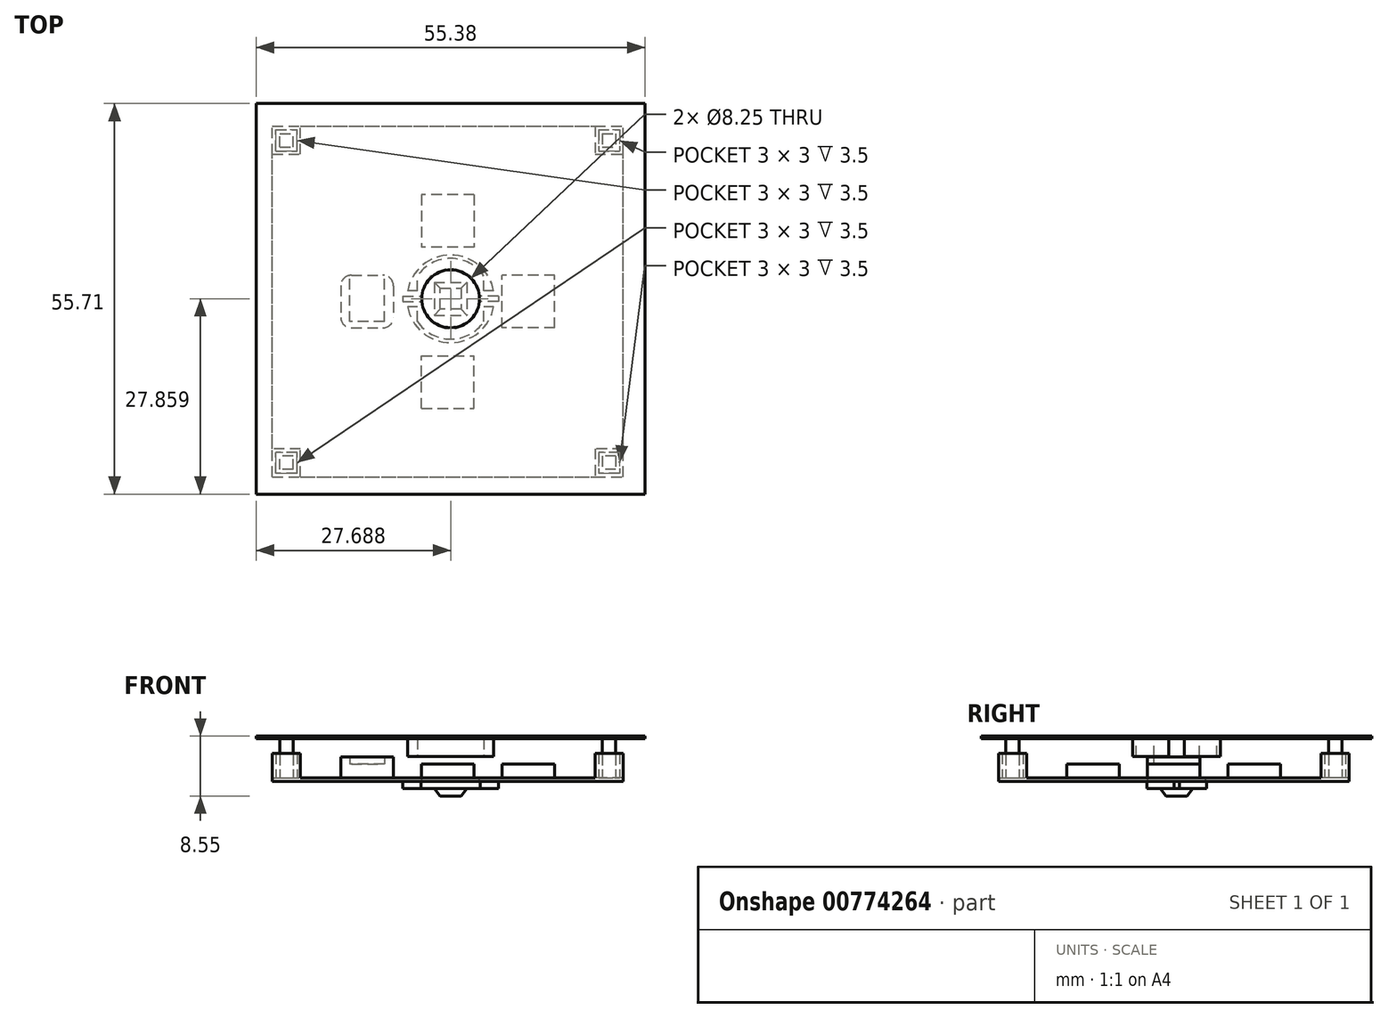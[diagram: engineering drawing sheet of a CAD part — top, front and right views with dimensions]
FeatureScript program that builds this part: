
annotation { "Feature Type Name" : "Feature", "Feature Type Description" : "" }
export const myFeature = defineFeature(function(context is Context, id is Id, definition is map)
    precondition{}
    {
        {
            var Q0;
            Q0=qCreatedBy(makeId("Top.planeOp"),FACE);
            var sketch = newSketch(context, id + "F0", { "sketchPlane" : qUnion([Q0])});
            skLineSegment(sketch, "E0.bottom", {"start": v(0, 0) * mm, "end": v(50, 0) * mm});
            skLineSegment(sketch, "E0.top", {"start": v(0, 50) * mm, "end": v(50, 50) * mm});
            skLineSegment(sketch, "E0.left", {"start": v(0, 0) * mm, "end": v(0, 50) * mm});
            skLineSegment(sketch, "E0.right", {"start": v(50, 0) * mm, "end": v(50, 50) * mm});
            skSolve(sketch);
        }
        {
            var Q0;
            Q0=makeQuery(id+"F0.imprint","IMPRINT",FACE,{"disambiguationData":[TD([[makeQuery(id+"F0.imprint","IMPRINT",EDGE,{"derivedFrom":sQuery(id+"F0.wireOp",EDGE,"E0.bottom")}),1.0]])]});
            extrude(context, id + "F1", {"entities" : qUnion([Q0]), "depth" : 0.5 * mm, "offsetDistance" : 25 * mm});
        }
        {
            var Q0;
            Q0=makeQuery(id+"F1.opExtrude","CAP_FACE",FACE,{"disambiguationData":[OSD([sQuery(id+"F0.wireOp",EDGE,"E0.bottom"),sQuery(id+"F0.wireOp",EDGE,"E0.top"),sQuery(id+"F0.wireOp",EDGE,"E0.left"),sQuery(id+"F0.wireOp",EDGE,"E0.right")])],"isStart":false});
            var sketch = newSketch(context, id + "F2", { "sketchPlane" : qUnion([Q0])});
            skLineSegment(sketch, "E1.bottom", {"start": v(46.5, 49.5) * mm, "end": v(49.5, 49.5) * mm});
            skLineSegment(sketch, "E1.top", {"start": v(46.5, 46.5) * mm, "end": v(49.5, 46.5) * mm});
            skLineSegment(sketch, "E1.left", {"start": v(46.5, 49.5) * mm, "end": v(46.5, 46.5) * mm});
            skLineSegment(sketch, "E1.right", {"start": v(49.5, 49.5) * mm, "end": v(49.5, 46.5) * mm});
            skPoint(sketch, "E2.middle.positionSnap0", {"position": v(49.5, 48) * mm});
            skPoint(sketch, "E2.middle.positionSnap1", {"position": v(48, 49.5) * mm});
            skPoint(sketch, "E2.centerSnap0", {"position": v(49.5, 48) * mm});
            skPoint(sketch, "E2.centerSnap1", {"position": v(48, 49.5) * mm});
            skLineSegment(sketch, "E3.0", {"start": v(46, 50) * mm, "end": v(50, 50) * mm});
            skLineSegment(sketch, "E3.1", {"start": v(46, 50) * mm, "end": v(46, 46) * mm});
            skLineSegment(sketch, "E3.2", {"start": v(46, 46) * mm, "end": v(50, 46) * mm});
            skLineSegment(sketch, "E3.3", {"start": v(50, 50) * mm, "end": v(50, 46) * mm});
            skLineSegment(sketch, "E4.0", {"start": v(47.05, 48.95) * mm, "end": v(48.95, 48.95) * mm});
            skLineSegment(sketch, "E4.1", {"start": v(47.05, 48.95) * mm, "end": v(47.05, 47.05) * mm});
            skLineSegment(sketch, "E4.2", {"start": v(47.05, 47.05) * mm, "end": v(48.95, 47.05) * mm});
            skLineSegment(sketch, "E4.3", {"start": v(48.95, 48.95) * mm, "end": v(48.95, 47.05) * mm});
            skLineSegment(sketch, "E5.1.0", {"start": v(0, 50) * mm, "end": v(4, 50) * mm});
            skLineSegment(sketch, "E5.1.1", {"start": v(4, 46) * mm, "end": v(4, 50) * mm});
            skLineSegment(sketch, "E5.1.2", {"start": v(0, 46) * mm, "end": v(4, 46) * mm});
            skLineSegment(sketch, "E5.1.3", {"start": v(1.05, 47.05) * mm, "end": v(2.95, 47.05) * mm});
            skLineSegment(sketch, "E5.1.4", {"start": v(3.5, 46.5) * mm, "end": v(3.5, 49.5) * mm});
            skLineSegment(sketch, "E5.1.5", {"start": v(0, 46) * mm, "end": v(0, 50) * mm});
            skLineSegment(sketch, "E5.1.6", {"start": v(2.95, 47.05) * mm, "end": v(2.95, 48.95) * mm});
            skLineSegment(sketch, "E5.1.7", {"start": v(0.5, 46.5) * mm, "end": v(3.5, 46.5) * mm});
            skPoint(sketch, "E5.1.8", {"position": v(2, 49.5) * mm});
            skLineSegment(sketch, "E5.1.9", {"start": v(1.05, 47.05) * mm, "end": v(1.05, 48.95) * mm});
            skPoint(sketch, "E5.1.10", {"position": v(0.5, 48) * mm});
            skPoint(sketch, "E5.1.11", {"position": v(2, 49.5) * mm});
            skLineSegment(sketch, "E5.1.12", {"start": v(0.5, 46.5) * mm, "end": v(0.5, 49.5) * mm});
            skPoint(sketch, "E5.1.13", {"position": v(0.5, 48) * mm});
            skLineSegment(sketch, "E5.1.14", {"start": v(1.05, 48.95) * mm, "end": v(2.95, 48.95) * mm});
            skLineSegment(sketch, "E5.1.15", {"start": v(0.5, 49.5) * mm, "end": v(3.5, 49.5) * mm});
            skLineSegment(sketch, "E5.2.0", {"start": v(0, 0) * mm, "end": v(0, 4) * mm});
            skLineSegment(sketch, "E5.2.1", {"start": v(4, 4) * mm, "end": v(0, 4) * mm});
            skLineSegment(sketch, "E5.2.2", {"start": v(4, 0) * mm, "end": v(4, 4) * mm});
            skLineSegment(sketch, "E5.2.3", {"start": v(2.95, 1.05) * mm, "end": v(2.95, 2.95) * mm});
            skLineSegment(sketch, "E5.2.4", {"start": v(3.5, 3.5) * mm, "end": v(0.5, 3.5) * mm});
            skLineSegment(sketch, "E5.2.5", {"start": v(4, 0) * mm, "end": v(0, 0) * mm});
            skLineSegment(sketch, "E5.2.6", {"start": v(2.95, 2.95) * mm, "end": v(1.05, 2.95) * mm});
            skLineSegment(sketch, "E5.2.7", {"start": v(3.5, 0.5) * mm, "end": v(3.5, 3.5) * mm});
            skPoint(sketch, "E5.2.8", {"position": v(0.5, 2) * mm});
            skLineSegment(sketch, "E5.2.9", {"start": v(2.95, 1.05) * mm, "end": v(1.05, 1.05) * mm});
            skPoint(sketch, "E5.2.10", {"position": v(2, 0.5) * mm});
            skPoint(sketch, "E5.2.11", {"position": v(0.5, 2) * mm});
            skLineSegment(sketch, "E5.2.12", {"start": v(3.5, 0.5) * mm, "end": v(0.5, 0.5) * mm});
            skPoint(sketch, "E5.2.13", {"position": v(2, 0.5) * mm});
            skLineSegment(sketch, "E5.2.14", {"start": v(1.05, 1.05) * mm, "end": v(1.05, 2.95) * mm});
            skLineSegment(sketch, "E5.2.15", {"start": v(0.5, 0.5) * mm, "end": v(0.5, 3.5) * mm});
            skLineSegment(sketch, "E5.3.0", {"start": v(50, 0) * mm, "end": v(46, 0) * mm});
            skLineSegment(sketch, "E5.3.1", {"start": v(46, 4) * mm, "end": v(46, 0) * mm});
            skLineSegment(sketch, "E5.3.2", {"start": v(50, 4) * mm, "end": v(46, 4) * mm});
            skLineSegment(sketch, "E5.3.3", {"start": v(48.95, 2.95) * mm, "end": v(47.05, 2.95) * mm});
            skLineSegment(sketch, "E5.3.4", {"start": v(46.5, 3.5) * mm, "end": v(46.5, 0.5) * mm});
            skLineSegment(sketch, "E5.3.5", {"start": v(50, 4) * mm, "end": v(50, 0) * mm});
            skLineSegment(sketch, "E5.3.6", {"start": v(47.05, 2.95) * mm, "end": v(47.05, 1.05) * mm});
            skLineSegment(sketch, "E5.3.7", {"start": v(49.5, 3.5) * mm, "end": v(46.5, 3.5) * mm});
            skPoint(sketch, "E5.3.8", {"position": v(48, 0.5) * mm});
            skLineSegment(sketch, "E5.3.9", {"start": v(48.95, 2.95) * mm, "end": v(48.95, 1.05) * mm});
            skPoint(sketch, "E5.3.10", {"position": v(49.5, 2) * mm});
            skPoint(sketch, "E5.3.11", {"position": v(48, 0.5) * mm});
            skLineSegment(sketch, "E5.3.12", {"start": v(49.5, 3.5) * mm, "end": v(49.5, 0.5) * mm});
            skPoint(sketch, "E5.3.13", {"position": v(49.5, 2) * mm});
            skLineSegment(sketch, "E5.3.14", {"start": v(48.95, 1.05) * mm, "end": v(47.05, 1.05) * mm});
            skLineSegment(sketch, "E5.3.15", {"start": v(49.5, 0.5) * mm, "end": v(46.5, 0.5) * mm});
            skPoint(sketch, "E5.center", {"position": v(25, 25) * mm});
            skSolve(sketch);
        }
        {
            var Q0;
            Q0=makeQuery(id+"F2.imprint","IMPRINT",FACE,{"disambiguationData":[TD([[makeQuery(id+"F2.imprint","IMPRINT",EDGE,{"derivedFrom":sQuery(id+"F2.wireOp",EDGE,"E1.bottom")}),1.0]])]});
            var Q1;
            Q1=makeQuery(id+"F2.imprint","IMPRINT",FACE,{"disambiguationData":[TD([[makeQuery(id+"F2.imprint","IMPRINT",EDGE,{"derivedFrom":sQuery(id+"F2.wireOp",EDGE,"E5.1.0")}),-1.0]])]});
            var Q2;
            Q2=makeQuery(id+"F2.imprint","IMPRINT",FACE,{"disambiguationData":[TD([[makeQuery(id+"F2.imprint","IMPRINT",EDGE,{"derivedFrom":sQuery(id+"F2.wireOp",EDGE,"E5.2.0")}),-1.0]])]});
            var Q3;
            Q3=makeQuery(id+"F2.imprint","IMPRINT",FACE,{"disambiguationData":[TD([[makeQuery(id+"F2.imprint","IMPRINT",EDGE,{"derivedFrom":sQuery(id+"F2.wireOp",EDGE,"E5.3.0")}),-1.0]])]});
            var Q4;
            Q4=makeQuery(id+"F2.imprint","IMPRINT",FACE,{"disambiguationData":[TD([[makeQuery(id+"F2.imprint","IMPRINT",EDGE,{"derivedFrom":sQuery(id+"F2.wireOp",EDGE,"E5.3.0")}),1.0]])]});
            extrude(context, id + "F3", {"entities" : qUnion([Q0, Q1, Q2, Q3, Q4]), "operationType" : NewBodyOperationType.ADD, "depth" : 3.5 * mm, "offsetDistance" : 25 * mm});
        }
        {
            var Q0;
            Q0=makeQuery(id+"F2.imprint","IMPRINT",FACE,{"disambiguationData":[TD([[makeQuery(id+"F2.imprint","IMPRINT",EDGE,{"derivedFrom":sQuery(id+"F2.wireOp",EDGE,"E5.1.3")}),1.0]])]});
            var Q1;
            Q1=makeQuery(id+"F2.imprint","IMPRINT",FACE,{"disambiguationData":[TD([[makeQuery(id+"F2.imprint","IMPRINT",EDGE,{"derivedFrom":sQuery(id+"F2.wireOp",EDGE,"E4.0")}),-1.0]])]});
            var Q2;
            Q2=makeQuery(id+"F2.imprint","IMPRINT",FACE,{"disambiguationData":[TD([[makeQuery(id+"F2.imprint","IMPRINT",EDGE,{"derivedFrom":sQuery(id+"F2.wireOp",EDGE,"E5.3.3")}),1.0]])]});
            var Q3;
            Q3=makeQuery(id+"F2.imprint","IMPRINT",FACE,{"disambiguationData":[TD([[makeQuery(id+"F2.imprint","IMPRINT",EDGE,{"derivedFrom":sQuery(id+"F2.wireOp",EDGE,"E5.2.3")}),1.0]])]});
            extrude(context, id + "F4", {"entities" : qUnion([Q0, Q1, Q2, Q3]), "depth" : 6 * mm, "offsetDistance" : 25 * mm});
        }
        {
            var Q0;
            Q0=makeQuery(id+"F4.opExtrude","CAP_FACE",FACE,{"disambiguationData":[OSD([sQuery(id+"F2.wireOp",EDGE,"E4.0"),sQuery(id+"F2.wireOp",EDGE,"E4.1"),sQuery(id+"F2.wireOp",EDGE,"E4.2"),sQuery(id+"F2.wireOp",EDGE,"E4.3")])],"isStart":false});
            var sketch = newSketch(context, id + "F5", { "sketchPlane" : qUnion([Q0])});
            skLineSegment(sketch, "E6.bottom", {"start": v(53.1, 53.25) * mm, "end": v(-2.28, 53.25) * mm});
            skLineSegment(sketch, "E6.top", {"start": v(53.1, -2.46) * mm, "end": v(-2.28, -2.46) * mm});
            skLineSegment(sketch, "E6.left", {"start": v(53.1, 53.25) * mm, "end": v(53.1, -2.46) * mm});
            skLineSegment(sketch, "E6.right", {"start": v(-2.28, 53.25) * mm, "end": v(-2.28, -2.46) * mm});
            skSolve(sketch);
        }
        {
            var Q0;
            Q0=makeQuery(id+"F5.imprint","IMPRINT",FACE,{"disambiguationData":[TD([[makeQuery(id+"F5.imprint","IMPRINT",EDGE,{"derivedFrom":sQuery(id+"F5.wireOp",EDGE,"E6.bottom")}),1.0]])]});
            extrude(context, id + "F6", {"entities" : qUnion([Q0]), "operationType" : NewBodyOperationType.ADD, "oppositeDirection" : true, "depth" : 0.4 * mm, "offsetDistance" : 25 * mm});
        }
        {
            var Q0;
            {var subQ0=sQuery(id+"F2.wireOp",EDGE,"E4.3");var subQ1=sQuery(id+"F2.wireOp",EDGE,"E4.2");var subQ2=sQuery(id+"F2.wireOp",EDGE,"E4.1");var subQ3=sQuery(id+"F2.wireOp",EDGE,"E4.0");Q0=makeQuery(id+"F6.boolean.opBoolean","MERGE",FACE,{"derivedFrom":[makeQuery(id+"F4.opExtrude","CAP_FACE",FACE,{"disambiguationData":[OSD([subQ3,subQ2,subQ1,subQ0])],"isStart":false}),makeQuery(id+"F4.opExtrude","CAP_FACE",FACE,{"disambiguationData":[OSD([sQuery(id+"F2.wireOp",EDGE,"E5.1.3"),sQuery(id+"F2.wireOp",EDGE,"E5.1.6"),sQuery(id+"F2.wireOp",EDGE,"E5.1.9"),sQuery(id+"F2.wireOp",EDGE,"E5.1.14")])],"isStart":false}),makeQuery(id+"F4.opExtrude","CAP_FACE",FACE,{"disambiguationData":[OSD([sQuery(id+"F2.wireOp",EDGE,"E5.2.3"),sQuery(id+"F2.wireOp",EDGE,"E5.2.6"),sQuery(id+"F2.wireOp",EDGE,"E5.2.9"),sQuery(id+"F2.wireOp",EDGE,"E5.2.14")])],"isStart":false}),makeQuery(id+"F4.opExtrude","CAP_FACE",FACE,{"disambiguationData":[OSD([sQuery(id+"F2.wireOp",EDGE,"E5.3.3"),sQuery(id+"F2.wireOp",EDGE,"E5.3.6"),sQuery(id+"F2.wireOp",EDGE,"E5.3.9"),sQuery(id+"F2.wireOp",EDGE,"E5.3.14")])],"isStart":false}),makeQuery(id+"F6.opExtrude","CAP_FACE",FACE,{"disambiguationData":[OSD([subQ3,subQ2,subQ1,subQ0,sQuery(id+"F5.wireOp",EDGE,"E6.bottom"),sQuery(id+"F5.wireOp",EDGE,"E6.top"),sQuery(id+"F5.wireOp",EDGE,"E6.left"),sQuery(id+"F5.wireOp",EDGE,"E6.right")])],"isStart":true})]});}
            var sketch = newSketch(context, id + "F7", { "sketchPlane" : qUnion([Q0])});
            skCircle(sketch, "E7", {"center": v(25.4, 25.4) * mm, "radius": 4.12 * mm});
            skPoint(sketch, "E7.centerSnap0", {"position": v(25.4, 53.25) * mm});
            skPoint(sketch, "E7.centerSnap1", {"position": v(53.1, 25.4) * mm});
            skSolve(sketch);
        }
        {
            var Q0;
            Q0=makeQuery(id+"F7.imprint","IMPRINT",FACE,{"disambiguationData":[TD([[makeQuery(id+"F7.imprint","IMPRINT",EDGE,{"derivedFrom":sQuery(id+"F7.wireOp",EDGE,"E7")}),1.0]])]});
            extrude(context, id + "F8", {"entities" : qUnion([Q0]), "operationType" : NewBodyOperationType.REMOVE, "oppositeDirection" : true, "depth" : 25 * mm, "offsetDistance" : 25 * mm});
        }
        {
            var Q0;
            Q0=makeQuery(id+"FnoxdWEcKo2KXdU_3.boolean.opBoolean","MERGE",FACE,{"derivedFrom":[makeQuery(id+"F6.opExtrude","CAP_FACE",FACE,{"disambiguationData":[OSD([sQuery(id+"F2.wireOp",EDGE,"E4.0"),sQuery(id+"F2.wireOp",EDGE,"E4.1"),sQuery(id+"F2.wireOp",EDGE,"E4.2"),sQuery(id+"F2.wireOp",EDGE,"E4.3"),sQuery(id+"F5.wireOp",EDGE,"E6.bottom"),sQuery(id+"F5.wireOp",EDGE,"E6.top"),sQuery(id+"F5.wireOp",EDGE,"E6.left"),sQuery(id+"F5.wireOp",EDGE,"E6.right")])],"isStart":false}),makeQuery(id+"FnoxdWEcKo2KXdU_3.opExtrude","SWEPT_FACE",FACE,{"disambiguationData":[OSD([sQuery(id+"F0zA4uYZW5pRUPb_3.wireOp",EDGE,"ZhX8Fjgi-kqvp-VlpE-l4Rn-IeRyZbtZChRy.bottom")])]})]});
            var sketch = newSketch(context, id + "F9", { "sketchPlane" : qUnion([Q0])});
            skLineSegment(sketch, "E8", {"start": v(25.4, -25.4) * mm, "end": v(29.53, -25.4) * mm});
            skCircle(sketch, "E9", {"center": v(25.4, -25.4) * mm, "radius": 5.75 * mm});
            skCircle(sketch, "E10", {"center": v(25.4, -25.4) * mm, "radius": 6.25 * mm});
            skLineSegment(sketch, "E11", {"start": v(30.16, -22.16) * mm, "end": v(30.16, -28.64) * mm});
            skLineSegment(sketch, "E12", {"start": v(20.66, -22.16) * mm, "end": v(20.66, -28.64) * mm});
            skSolve(sketch);
        }
        {
            var Q0;
            {var subQ0=sQuery(id+"F9.wireOp",EDGE,"scZHxu3C-Op0m-khkx-aFYf-Y6gfYPpbK4Jl");Q0=makeQuery(id+"F9.imprint","IMPRINT",FACE,{"disambiguationData":[TD([[makeQuery(id+"F9.imprint","IMPRINT",EDGE,{"derivedFrom":subQ0}),-1.0]])]});}
            var Q1;
            Q1=makeQuery(id+"F9.imprint","IMPRINT",FACE,{"disambiguationData":[TD([[makeQuery(id+"F9.imprint","IMPRINT",EDGE,{"derivedFrom":sQuery(id+"F9.wireOp",EDGE,"TZnjQXDI-6Li4-iHBg-k0Ms-UXLXTafPAAUR")}),-1.0]])]});
            var Q2;
            {var subQ5=sQuery(id+"F9.wireOp",EDGE,"F097BGmS-OGrE-Bj6g-8D74-8TD7AIuaI6WG");Q2=makeQuery(id+"F9.imprint","IMPRINT",FACE,{"disambiguationData":[TD([[makeQuery(id+"F9.imprint","IMPRINT",EDGE,{"derivedFrom":subQ5}),1.0]])]});}
            var Q3;
            {var subQ0=sQuery(id+"F9.wireOp",EDGE,"7kH5QydC-Tvzd-wKTz-Q8G2-IkZKPWhglS4Q");Q3=makeQuery(id+"F9.imprint","IMPRINT",FACE,{"disambiguationData":[TD([[makeQuery(id+"F9.imprint","IMPRINT",EDGE,{"derivedFrom":subQ0}),-1.0]])]});}
            var Q4;
            Q4=makeQuery(id+"F9.imprint","IMPRINT",FACE,{"disambiguationData":[TD([[makeQuery(id+"F9.imprint","IMPRINT",EDGE,{"derivedFrom":sQuery(id+"F9.wireOp",EDGE,"E10")}),1.0]])]});
            var Q5;
            {var subQ0=sQuery(id+"F9.wireOp",EDGE,"E11");Q5=makeQuery(id+"F9.imprint","IMPRINT",FACE,{"disambiguationData":[TD([[makeQuery(id+"F9.imprint","IMPRINT",EDGE,{"derivedFrom":subQ0}),1.0]])]});}
            var Q6;
            {var subQ0=sQuery(id+"F9.wireOp",EDGE,"XEGzPRrg-yoOm-QcLb-v5r6-et9ivG9pCGP1");Q6=makeQuery(id+"F9.imprint","IMPRINT",FACE,{"disambiguationData":[TD([[makeQuery(id+"F9.imprint","IMPRINT",EDGE,{"derivedFrom":subQ0}),1.0]])]});}
            var Q7;
            {var subQ0=sQuery(id+"F9.wireOp",EDGE,"23869d93-fd9b-4a96-a758-ed1db567c41d");Q7=makeQuery(id+"F9.imprint","IMPRINT",FACE,{"disambiguationData":[TD([[makeQuery(id+"F9.imprint","IMPRINT",EDGE,{"derivedFrom":subQ0}),-1.0]])]});}
            var Q8;
            {var subQ0=sQuery(id+"F9.wireOp",EDGE,"E12");Q8=makeQuery(id+"F9.imprint","IMPRINT",FACE,{"disambiguationData":[TD([[makeQuery(id+"F9.imprint","IMPRINT",EDGE,{"derivedFrom":subQ0}),-1.0]])]});}
            extrude(context, id + "F10", {"entities" : qUnion([Q0, Q1, Q2, Q3, Q4, Q5, Q6, Q7, Q8]), "operationType" : NewBodyOperationType.ADD, "depth" : 2.5 * mm, "offsetDistance" : 25 * mm});
        }
        {
            var Q0;
            {var subQ0=sQuery(id+"F0.wireOp",EDGE,"E0.bottom");var subQ1=sQuery(id+"F0.wireOp",EDGE,"E0.right");var subQ2=sQuery(id+"F0.wireOp",EDGE,"E0.top");var subQ3=sQuery(id+"F0.wireOp",EDGE,"E0.left");Q0=makeQuery(id+"F3.boolean.opBoolean","SPLIT",FACE,{"disambiguationData":[TD([makeQuery(id+"F1.opExtrude","SWEPT_FACE",FACE,{"disambiguationData":[OSD([subQ0])]})])],"derivedFrom":makeQuery(id+"F1.opExtrude","CAP_FACE",FACE,{"disambiguationData":[OSD([subQ0,subQ2,subQ3,subQ1])],"isStart":false})});}
            var sketch = newSketch(context, id + "F11", { "sketchPlane" : qUnion([Q0])});
            skLineSegment(sketch, "E13.bottom", {"start": v(9.75, 28.75) * mm, "end": v(17.25, 28.75) * mm});
            skLineSegment(sketch, "E13.top", {"start": v(9.75, 21.25) * mm, "end": v(17.25, 21.25) * mm});
            skLineSegment(sketch, "E13.left", {"start": v(9.75, 28.75) * mm, "end": v(9.75, 21.25) * mm});
            skLineSegment(sketch, "E13.right", {"start": v(17.25, 28.75) * mm, "end": v(17.25, 21.25) * mm});
            skPoint(sketch, "E13.middle.positionSnap0", {"position": v(0, 25) * mm});
            skPoint(sketch, "E13.middle.positionSnap1", {"position": v(25, 0) * mm});
            skPoint(sketch, "E13.centerSnap0", {"position": v(0, 25) * mm});
            skPoint(sketch, "E13.centerSnap1", {"position": v(25, 0) * mm});
            skPoint(sketch, "E14", {"position": v(13.5, 25) * mm});
            skPoint(sketch, "E15", {"position": v(13.5, 21.25) * mm});
            skPoint(sketch, "E16", {"position": v(17.25, 25) * mm});
            skLineSegment(sketch, "E17", {"start": v(0, 25) * mm, "end": v(25, 25) * mm});
            skPoint(sketch, "E17.endSnap0", {"position": v(25, 50) * mm});
            skLineSegment(sketch, "E18.1.0", {"start": v(21.25, 9.75) * mm, "end": v(21.25, 17.25) * mm});
            skLineSegment(sketch, "E18.1.1", {"start": v(21.25, 9.75) * mm, "end": v(28.75, 9.75) * mm});
            skLineSegment(sketch, "E18.1.2", {"start": v(21.25, 17.25) * mm, "end": v(28.75, 17.25) * mm});
            skLineSegment(sketch, "E18.1.3", {"start": v(28.75, 9.75) * mm, "end": v(28.75, 17.25) * mm});
            skLineSegment(sketch, "E18.2.0", {"start": v(40.25, 21.25) * mm, "end": v(32.75, 21.25) * mm});
            skLineSegment(sketch, "E18.2.1", {"start": v(40.25, 21.25) * mm, "end": v(40.25, 28.75) * mm});
            skLineSegment(sketch, "E18.2.2", {"start": v(32.75, 21.25) * mm, "end": v(32.75, 28.75) * mm});
            skLineSegment(sketch, "E18.2.3", {"start": v(40.25, 28.75) * mm, "end": v(32.75, 28.75) * mm});
            skLineSegment(sketch, "E18.3.0", {"start": v(28.75, 40.25) * mm, "end": v(28.75, 32.75) * mm});
            skLineSegment(sketch, "E18.3.1", {"start": v(28.75, 40.25) * mm, "end": v(21.25, 40.25) * mm});
            skLineSegment(sketch, "E18.3.2", {"start": v(28.75, 32.75) * mm, "end": v(21.25, 32.75) * mm});
            skLineSegment(sketch, "E18.3.3", {"start": v(21.25, 40.25) * mm, "end": v(21.25, 32.75) * mm});
            skPoint(sketch, "E18.center", {"position": v(25, 25) * mm});
            skSolve(sketch);
        }
        {
            var Q0;
            Q0=makeQuery(id+"F11.imprint","IMPRINT",FACE,{"disambiguationData":[TD([[makeQuery(id+"F11.imprint","IMPRINT",EDGE,{"derivedFrom":sQuery(id+"F11.wireOp",EDGE,"E13.bottom")}),-1.0]])]});
            var Q1;
            {var subQ0=sQuery(id+"F11.wireOp",EDGE,"E13.top");Q1=makeQuery(id+"F11.imprint","IMPRINT",FACE,{"disambiguationData":[TD([[makeQuery(id+"F11.imprint","IMPRINT",EDGE,{"derivedFrom":subQ0}),1.0]])]});}
            var Q2;
            Q2=makeQuery(id+"F11.imprint","IMPRINT",FACE,{"disambiguationData":[TD([[makeQuery(id+"F11.imprint","IMPRINT",EDGE,{"derivedFrom":sQuery(id+"F11.wireOp",EDGE,"E18.1.0")}),-1.0]])]});
            var Q3;
            Q3=makeQuery(id+"F11.imprint","IMPRINT",FACE,{"disambiguationData":[TD([[makeQuery(id+"F11.imprint","IMPRINT",EDGE,{"derivedFrom":sQuery(id+"F11.wireOp",EDGE,"E18.2.0")}),-1.0]])]});
            var Q4;
            Q4=makeQuery(id+"F11.imprint","IMPRINT",FACE,{"disambiguationData":[TD([[makeQuery(id+"F11.imprint","IMPRINT",EDGE,{"derivedFrom":sQuery(id+"F11.wireOp",EDGE,"E18.3.0")}),-1.0]])]});
            extrude(context, id + "F12", {"entities" : qUnion([Q0, Q1, Q2, Q3, Q4]), "operationType" : NewBodyOperationType.ADD, "depth" : 2 * mm, "offsetDistance" : 25 * mm});
        }
        {
            var Q0;
            Q0=makeQuery(id+"F12.opExtrude","CAP_FACE",FACE,{"disambiguationData":[OSD([sQuery(id+"F11.wireOp",EDGE,"E13.bottom"),sQuery(id+"F11.wireOp",EDGE,"E13.top"),sQuery(id+"F11.wireOp",EDGE,"E13.left"),sQuery(id+"F11.wireOp",EDGE,"E13.right")])],"isStart":false});
            var sketch = newSketch(context, id + "F13", { "sketchPlane" : qUnion([Q0])});
            skLineSegment(sketch, "E19", {"start": v(15.97, 21.25) * mm, "end": v(15.97, 28.75) * mm});
            skLineSegment(sketch, "E20", {"start": v(11.02, 21.25) * mm, "end": v(11.02, 28.75) * mm});
            skLineSegment(sketch, "E21", {"start": v(11.02, 25) * mm, "end": v(9.75, 25) * mm, "construction": true});
            skLineSegment(sketch, "E22", {"start": v(15.97, 25) * mm, "end": v(17.25, 25) * mm, "construction": true});
            skLineSegment(sketch, "E23", {"start": v(15.97, 22.12) * mm, "end": v(11.02, 22.12) * mm});
            skSolve(sketch);
        }
        {
            var Q0;
            {var subQ0=makeQuery(id+"F12.opExtrude","CAP_EDGE",EDGE,{"disambiguationData":[OSD([sQuery(id+"F11.wireOp",EDGE,"E13.right")])],"isStart":false});Q0=makeQuery(id+"F13.imprint","IMPRINT",FACE,{"disambiguationData":[TD([[makeQuery(id+"F13.imprint","IMPRINT",EDGE,{"derivedFrom":subQ0}),-1.0]])]});}
            var Q1;
            {var subQ3=sQuery(id+"F13.wireOp",EDGE,"E23");Q1=makeQuery(id+"F13.imprint","IMPRINT",FACE,{"disambiguationData":[TD([[makeQuery(id+"F13.imprint","IMPRINT",EDGE,{"derivedFrom":subQ3}),1.0]])]});}
            var Q2;
            {var subQ0=makeQuery(id+"F12.opExtrude","CAP_EDGE",EDGE,{"disambiguationData":[OSD([sQuery(id+"F11.wireOp",EDGE,"E13.left")])],"isStart":false});Q2=makeQuery(id+"F13.imprint","IMPRINT",FACE,{"disambiguationData":[TD([[makeQuery(id+"F13.imprint","IMPRINT",EDGE,{"derivedFrom":subQ0}),1.0]])]});}
            extrude(context, id + "F14", {"entities" : qUnion([Q0, Q1, Q2]), "operationType" : NewBodyOperationType.ADD, "depth" : 1 * mm, "offsetDistance" : 25 * mm});
        }
        {
            var Q0;
            {var subQ0=sQuery(id+"F11.wireOp",EDGE,"E13.left");var subQ1=sQuery(id+"F11.wireOp",EDGE,"E13.bottom");Q0=makeQuery(id+"F14.boolean.opBoolean","MERGE",EDGE,{"derivedFrom":[makeQuery(id+"F12.opExtrude","SWEPT_EDGE",EDGE,{"disambiguationData":[OSD([subQ1,subQ0])]}),makeQuery(id+"F14.opExtrude","SWEPT_EDGE",EDGE,{"disambiguationData":[OSD([subQ1,subQ0])]})]});}
            var Q1;
            {var subQ0=sQuery(id+"F11.wireOp",EDGE,"E13.right");var subQ1=sQuery(id+"F11.wireOp",EDGE,"E13.bottom");Q1=makeQuery(id+"F14.boolean.opBoolean","MERGE",EDGE,{"derivedFrom":[makeQuery(id+"F12.opExtrude","SWEPT_EDGE",EDGE,{"disambiguationData":[OSD([subQ1,subQ0])]}),makeQuery(id+"F14.opExtrude","SWEPT_EDGE",EDGE,{"disambiguationData":[OSD([subQ1,subQ0])]})]});}
            var Q2;
            {var subQ0=sQuery(id+"F11.wireOp",EDGE,"E13.right");var subQ1=sQuery(id+"F11.wireOp",EDGE,"E13.top");Q2=makeQuery(id+"F14.boolean.opBoolean","MERGE",EDGE,{"derivedFrom":[makeQuery(id+"F12.opExtrude","SWEPT_EDGE",EDGE,{"disambiguationData":[OSD([subQ1,subQ0])]}),makeQuery(id+"F14.opExtrude","SWEPT_EDGE",EDGE,{"disambiguationData":[OSD([subQ1,subQ0])]})]});}
            var Q3;
            {var subQ0=sQuery(id+"F11.wireOp",EDGE,"E13.left");var subQ1=sQuery(id+"F11.wireOp",EDGE,"E13.top");Q3=makeQuery(id+"F14.boolean.opBoolean","MERGE",EDGE,{"derivedFrom":[makeQuery(id+"F12.opExtrude","SWEPT_EDGE",EDGE,{"disambiguationData":[OSD([subQ1,subQ0])]}),makeQuery(id+"F14.opExtrude","SWEPT_EDGE",EDGE,{"disambiguationData":[OSD([subQ1,subQ0])]})]});}
            fillet(context, id + "F15", {"entities" : qUnion([Q0, Q1, Q2, Q3]), "radius" : 1.5 * mm, "tangentPropagation" : true, "allowEdgeOverflow" : false});
        }
        {
            var Q0;
            Q0=makeQuery(id+"F10.opExtrude","CAP_FACE",FACE,{"disambiguationData":[OSD([sQuery(id+"F9.wireOp",EDGE,"hR2DkXYq-zMif-uwH9-XGDZ-Vy1SFXDIvF5I"),sQuery(id+"F9.wireOp",EDGE,"TZnjQXDI-6Li4-iHBg-k0Ms-UXLXTafPAAUR"),sQuery(id+"F9.wireOp",EDGE,"E9"),sQuery(id+"F9.wireOp",EDGE,"E10"),sQuery(id+"F9.wireOp",EDGE,"HmTSUiL7-nfB5-YJrb-Olma-AtZkijcZXdec"),sQuery(id+"F9.wireOp",EDGE,"xdDC7rom-dxiO-1iCL-EjCq-CHcHlSsKxfgP"),sQuery(id+"F9.wireOp",EDGE,"7kH5QydC-Tvzd-wKTz-Q8G2-IkZKPWhglS4Q"),sQuery(id+"F9.wireOp",EDGE,"w4amh8i3-zfD1-aIUs-LVQh-Add8YU8KaKkI")])],"isStart":false});
            var sketch = newSketch(context, id + "F16", { "sketchPlane" : qUnion([Q0])});
            skLineSegment(sketch, "E24.bottom", {"start": v(32.9, -24.27) * mm, "end": v(17.9, -24.27) * mm});
            skLineSegment(sketch, "E24.top", {"start": v(32.9, -26.52) * mm, "end": v(17.9, -26.52) * mm});
            skLineSegment(sketch, "E24.left", {"start": v(32.9, -24.27) * mm, "end": v(32.9, -26.52) * mm});
            skLineSegment(sketch, "E24.right", {"start": v(17.9, -24.27) * mm, "end": v(17.9, -26.52) * mm});
            skPoint(sketch, "E24.middle", {"position": v(25.4, -25.4) * mm});
            skSolve(sketch);
        }
        {
            var Q0;
            Q0=qSketchRegion(id+"F16",true);
            var Q1;
            {var subQ0=sQuery(id+"F5.wireOp",EDGE,"E6.right");var subQ1=sQuery(id+"F2.wireOp",EDGE,"E4.0");var subQ2=sQuery(id+"F2.wireOp",EDGE,"E4.3");var subQ3=sQuery(id+"F2.wireOp",EDGE,"E4.1");var subQ4=sQuery(id+"F2.wireOp",EDGE,"E4.2");var subQ5=sQuery(id+"F5.wireOp",EDGE,"E6.bottom");var subQ6=sQuery(id+"F5.wireOp",EDGE,"E6.top");var subQ7=sQuery(id+"F5.wireOp",EDGE,"E6.left");Q1=makeQuery(id+"F10.boolean.opBoolean","SPLIT",FACE,{"disambiguationData":[TD([makeQuery(id+"F4.opExtrude","SWEPT_FACE",FACE,{"disambiguationData":[OSD([subQ1])]})])],"derivedFrom":makeQuery(id+"F6.opExtrude","CAP_FACE",FACE,{"disambiguationData":[OSD([subQ1,subQ3,subQ4,subQ2,subQ5,subQ6,subQ7,subQ0])],"isStart":false})});}
            extrude(context, id + "F17", {"entities" : qUnion([Q0]), "operationType" : NewBodyOperationType.REMOVE, "endBound" : BoundingType.UP_TO_SURFACE, "oppositeDirection" : true, "depth" : 25 * mm, "endBoundEntityFace" : qUnion([Q1]), "offsetDistance" : 25 * mm});
        }
        {
            var Q0;
            Q0=qCreatedBy(makeId("Top.planeOp"),FACE);
            var sketch = newSketch(context, id + "F18", { "sketchPlane" : qUnion([Q0])});
            skCircle(sketch, "E25", {"center": v(25.4, 25.4) * mm, "radius": 4.25 * mm});
            skLineSegment(sketch, "E26", {"start": v(25.4, 25.4) * mm, "end": v(32.2, 25.4) * mm, "construction": true});
            skLineSegment(sketch, "E27", {"start": v(25.4, 25.4) * mm, "end": v(25.4, 29.65) * mm, "construction": true});
            skLineSegment(sketch, "E28", {"start": v(25.4, 25.4) * mm, "end": v(25.4, 21.15) * mm, "construction": true});
            skPoint(sketch, "E29.endSnap0", {"position": v(30.16, 23.22) * mm});
            skLineSegment(sketch, "E30", {"start": v(32.2, 25.02) * mm, "end": v(25.4, 25.02) * mm});
            skLineSegment(sketch, "E31", {"start": v(32.2, 23.22) * mm, "end": v(32.2, 25.02) * mm});
            skLineSegment(sketch, "E32.MirrorCS", {"start": v(32.2, 25.77) * mm, "end": v(25.4, 25.77) * mm});
            skLineSegment(sketch, "E33.MirrorCS", {"start": v(32.2, 27.58) * mm, "end": v(32.2, 25.77) * mm});
            skLineSegment(sketch, "E34.MirrorCS", {"start": v(18.61, 25.02) * mm, "end": v(25.4, 25.02) * mm});
            skLineSegment(sketch, "E35.MirrorCS", {"start": v(18.61, 23.22) * mm, "end": v(18.61, 25.02) * mm});
            skLineSegment(sketch, "E36.MirrorCS", {"start": v(18.61, 25.77) * mm, "end": v(25.4, 25.77) * mm});
            skLineSegment(sketch, "E37.MirrorCS", {"start": v(18.61, 27.58) * mm, "end": v(18.61, 25.77) * mm});
            skLineSegment(sketch, "E38", {"start": v(32.2, 23.22) * mm, "end": v(32.2, 23.22) * mm});
            skLineSegment(sketch, "E39", {"start": v(32.2, 23.22) * mm, "end": v(32.2, 25.4) * mm});
            skLineSegment(sketch, "E40.MirrorCS", {"start": v(32.2, 27.58) * mm, "end": v(32.2, 25.4) * mm});
            skLineSegment(sketch, "E41.MirrorCS", {"start": v(32.2, 27.58) * mm, "end": v(32.2, 27.58) * mm});
            skLineSegment(sketch, "E42.MirrorCS", {"start": v(18.61, 27.58) * mm, "end": v(18.61, 25.4) * mm});
            skLineSegment(sketch, "E43.MirrorCS", {"start": v(18.61, 27.58) * mm, "end": v(18.61, 27.58) * mm});
            skLineSegment(sketch, "E44.MirrorCS", {"start": v(18.61, 23.22) * mm, "end": v(18.61, 23.22) * mm});
            skLineSegment(sketch, "E45.MirrorCS", {"start": v(18.61, 23.22) * mm, "end": v(18.61, 25.4) * mm});
            skSolve(sketch);
        }
        {
            var Q0;
            Q0 = qSketchRegion(id + "F18", true);
            extrude(context, id + "F19", {"entities" : qUnion([Q0]), "oppositeDirection" : true, "depth" : 1 * mm, "offsetDistance" : 25 * mm});
        }
        {
            var Q0;
            Q0=makeQuery(id+"F19.opExtrude","CAP_FACE",FACE,{"disambiguationData":[OSD([sQuery(id+"F18.wireOp",EDGE,"E25"),sQuery(id+"F18.wireOp",EDGE,"E30"),sQuery(id+"F18.wireOp",EDGE,"E31"),sQuery(id+"F18.wireOp",EDGE,"E32.MirrorCS"),sQuery(id+"F18.wireOp",EDGE,"E34.MirrorCS"),sQuery(id+"F18.wireOp",EDGE,"E36.MirrorCS"),sQuery(id+"F18.wireOp",EDGE,"E38"),sQuery(id+"F18.wireOp",EDGE,"E39"),sQuery(id+"F18.wireOp",EDGE,"E40.MirrorCS"),sQuery(id+"F18.wireOp",EDGE,"E33.MirrorCS"),sQuery(id+"F18.wireOp",EDGE,"E41.MirrorCS"),sQuery(id+"F18.wireOp",EDGE,"E42.MirrorCS"),sQuery(id+"F18.wireOp",EDGE,"E43.MirrorCS"),sQuery(id+"F18.wireOp",EDGE,"E37.MirrorCS"),sQuery(id+"F18.wireOp",EDGE,"E35.MirrorCS"),sQuery(id+"F18.wireOp",EDGE,"E44.MirrorCS"),sQuery(id+"F18.wireOp",EDGE,"E45.MirrorCS")])],"isStart":false});
            var sketch = newSketch(context, id + "F20", { "sketchPlane" : qUnion([Q0])});
            skLineSegment(sketch, "E46.bottom", {"start": v(27.9, -22.9) * mm, "end": v(22.9, -22.9) * mm});
            skLineSegment(sketch, "E46.top", {"start": v(27.9, -27.9) * mm, "end": v(22.9, -27.9) * mm});
            skLineSegment(sketch, "E46.left", {"start": v(27.9, -22.9) * mm, "end": v(27.9, -27.9) * mm});
            skLineSegment(sketch, "E46.right", {"start": v(22.9, -22.9) * mm, "end": v(22.9, -27.9) * mm});
            skPoint(sketch, "E46.middle", {"position": v(25.4, -25.4) * mm});
            skSolve(sketch);
        }
        {
            var Q0;
            Q0=makeQuery(id+"F20.imprint","IMPRINT",FACE,{"disambiguationData":[TD([[makeQuery(id+"F20.imprint","IMPRINT",EDGE,{"derivedFrom":sQuery(id+"F20.wireOp",EDGE,"E46.bottom")}),1.0]])]});
            extrude(context, id + "F21", {"entities" : qUnion([Q0]), "operationType" : NewBodyOperationType.ADD, "depth" : 1.05 * mm, "offsetDistance" : 25 * mm});
        }
        {
            var Q0;
            Q0=makeQuery(id+"F21.opExtrude","CAP_FACE",FACE,{"disambiguationData":[OSD([sQuery(id+"F20.wireOp",EDGE,"E46.bottom"),sQuery(id+"F20.wireOp",EDGE,"E46.top"),sQuery(id+"F20.wireOp",EDGE,"E46.left"),sQuery(id+"F20.wireOp",EDGE,"E46.right")])],"isStart":false});
            chamfer(context, id + "F22", {"entities" : qUnion([Q0]), "chamferType" : ChamferType.TWO_OFFSETS, "width1" : 1 * mm, "oppositeDirection" : false, "width2" : 1.25 * mm, "tangentPropagation" : true});
        }
    });
